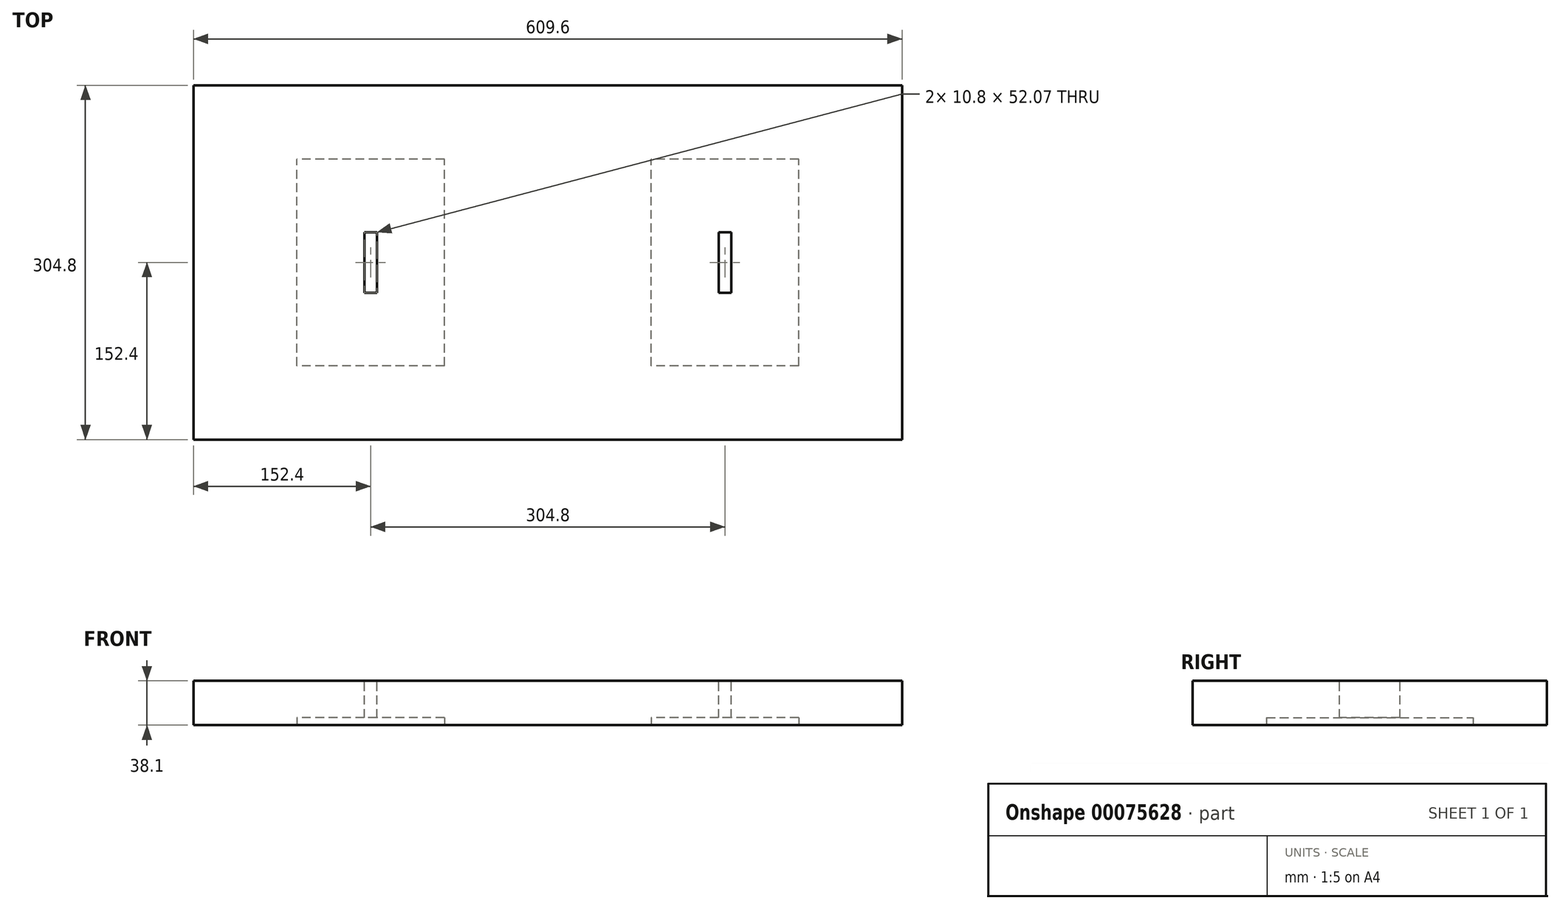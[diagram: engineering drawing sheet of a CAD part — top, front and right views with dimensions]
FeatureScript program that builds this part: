
annotation { "Feature Type Name" : "Feature", "Feature Type Description" : "" }
export const myFeature = defineFeature(function(context is Context, id is Id, definition is map)
    precondition{}
    {
        {
            var Q0;
            Q0=qCreatedBy(makeId("Top.planeOp"),FACE);
            var sketch = newSketch(context, id + "F0", { "sketchPlane" : qUnion([Q0])});
            skLineSegment(sketch, "E0.rect.bottom", {"start": v(304.8, 152.4) * mm, "end": v(-304.8, 152.4) * mm});
            skLineSegment(sketch, "E0.rect.top", {"start": v(304.8, -152.4) * mm, "end": v(-304.8, -152.4) * mm});
            skLineSegment(sketch, "E0.rect.left", {"start": v(304.8, 152.4) * mm, "end": v(304.8, -152.4) * mm});
            skLineSegment(sketch, "E0.rect.right", {"start": v(-304.8, 152.4) * mm, "end": v(-304.8, -152.4) * mm});
            skPoint(sketch, "E0.rect.middle", {"position": v(0, 0) * mm});
            skSolve(sketch);
        }
        {
            var Q0;
            Q0 = qSketchRegion(id + "F0", true);
            extrude(context, id + "F1", {"entities" : qUnion([Q0]), "endBound" : BoundingType.SYMMETRIC, "depth" : 38.1 * mm});
        }
        {
            var Q0;
            Q0=makeQuery(id+"F1.opExtrude","CAP_FACE",FACE,{"disambiguationData":[OSD([sQuery(id+"F0.wireOp",EDGE,"E0.rect.bottom"),sQuery(id+"F0.wireOp",EDGE,"E0.rect.top"),sQuery(id+"F0.wireOp",EDGE,"E0.rect.left"),sQuery(id+"F0.wireOp",EDGE,"E0.rect.right")])],"isStart":false});
            var sketch = newSketch(context, id + "F2", { "sketchPlane" : qUnion([Q0])});
            skLineSegment(sketch, "E1.rect.bottom", {"start": v(-147, 26.03) * mm, "end": v(-157.8, 26.03) * mm});
            skLineSegment(sketch, "E1.rect.top", {"start": v(-147, -26.04) * mm, "end": v(-157.8, -26.04) * mm});
            skLineSegment(sketch, "E1.rect.left", {"start": v(-147, 26.03) * mm, "end": v(-147, -26.04) * mm});
            skLineSegment(sketch, "E1.rect.right", {"start": v(-157.8, 26.03) * mm, "end": v(-157.8, -26.04) * mm});
            skPoint(sketch, "E1.rect.middle", {"position": v(-152.4, 0) * mm});
            skLineSegment(sketch, "E2.rect.bottom", {"start": v(157.8, 26.03) * mm, "end": v(147, 26.03) * mm});
            skLineSegment(sketch, "E2.rect.top", {"start": v(157.8, -26.04) * mm, "end": v(147, -26.04) * mm});
            skLineSegment(sketch, "E2.rect.left", {"start": v(157.8, 26.03) * mm, "end": v(157.8, -26.04) * mm});
            skLineSegment(sketch, "E2.rect.right", {"start": v(147, 26.03) * mm, "end": v(147, -26.04) * mm});
            skPoint(sketch, "E2.rect.middle", {"position": v(152.4, 0) * mm});
            skLineSegment(sketch, "E3", {"start": v(-152.4, 0) * mm, "end": v(152.4, 0) * mm, "construction": true});
            skSolve(sketch);
        }
        {
            var Q0;
            Q0 = qSketchRegion(id + "F2", true);
            extrude(context, id + "F3", {"entities" : qUnion([Q0]), "operationType" : NewBodyOperationType.REMOVE, "endBound" : BoundingType.THROUGH_ALL, "oppositeDirection" : true, "depth" : 25.4 * mm});
        }
        {
            var Q0;
            Q0=makeQuery(id+"F1.opExtrude","CAP_FACE",FACE,{"disambiguationData":[OSD([sQuery(id+"F0.wireOp",EDGE,"E0.rect.bottom"),sQuery(id+"F0.wireOp",EDGE,"E0.rect.top"),sQuery(id+"F0.wireOp",EDGE,"E0.rect.left"),sQuery(id+"F0.wireOp",EDGE,"E0.rect.right")])],"isStart":true});
            var sketch = newSketch(context, id + "F4", { "sketchPlane" : qUnion([Q0])});
            skLineSegment(sketch, "E4.rect.bottom", {"start": v(-88.9, 88.9) * mm, "end": v(-215.9, 88.9) * mm});
            skLineSegment(sketch, "E4.rect.top", {"start": v(-88.9, -88.9) * mm, "end": v(-215.9, -88.9) * mm});
            skLineSegment(sketch, "E4.rect.left", {"start": v(-88.9, 88.9) * mm, "end": v(-88.9, -88.9) * mm});
            skLineSegment(sketch, "E4.rect.right", {"start": v(-215.9, 88.9) * mm, "end": v(-215.9, -88.9) * mm});
            skPoint(sketch, "E4.rect.middle", {"position": v(-152.4, 0) * mm});
            skPoint(sketch, "E4.rect.middle.positionSnap0", {"position": v(-152.4, -26.03) * mm});
            skPoint(sketch, "E4.rect.middle.positionSnap1", {"position": v(-157.8, 0) * mm});
            skPoint(sketch, "E4.rect.centerSnap0", {"position": v(-152.4, -26.03) * mm});
            skPoint(sketch, "E4.rect.centerSnap1", {"position": v(-157.8, 0) * mm});
            skLineSegment(sketch, "E5.rect.bottom", {"start": v(215.9, 88.9) * mm, "end": v(88.9, 88.9) * mm});
            skLineSegment(sketch, "E5.rect.top", {"start": v(215.9, -88.9) * mm, "end": v(88.9, -88.9) * mm});
            skLineSegment(sketch, "E5.rect.left", {"start": v(215.9, 88.9) * mm, "end": v(215.9, -88.9) * mm});
            skLineSegment(sketch, "E5.rect.right", {"start": v(88.9, 88.9) * mm, "end": v(88.9, -88.9) * mm});
            skPoint(sketch, "E5.rect.middle", {"position": v(152.4, 0) * mm});
            skPoint(sketch, "E5.rect.middle.positionSnap0", {"position": v(152.4, -26.03) * mm});
            skPoint(sketch, "E5.rect.middle.positionSnap1", {"position": v(157.8, 0) * mm});
            skPoint(sketch, "E5.rect.centerSnap0", {"position": v(152.4, -26.03) * mm});
            skPoint(sketch, "E5.rect.centerSnap1", {"position": v(157.8, 0) * mm});
            skSolve(sketch);
        }
        {
            var Q0;
            Q0 = qSketchRegion(id + "F4", true);
            extrude(context, id + "F5", {"entities" : qUnion([Q0]), "operationType" : NewBodyOperationType.REMOVE, "oppositeDirection" : true, "depth" : 6.35 * mm});
        }
    });
